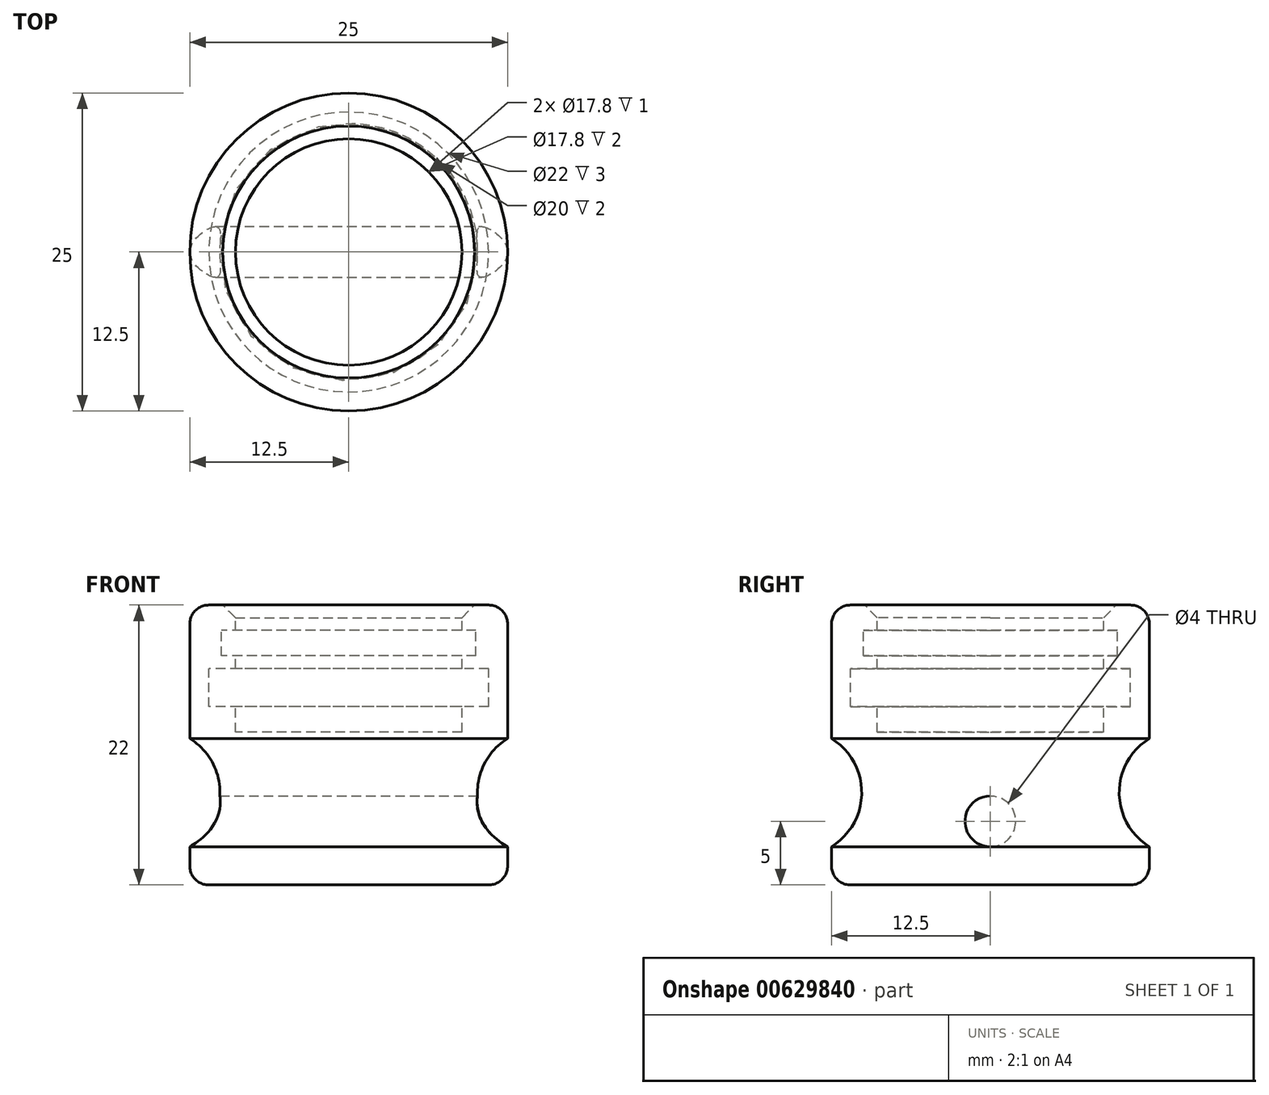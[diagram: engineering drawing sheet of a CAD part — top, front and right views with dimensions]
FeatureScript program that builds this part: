
annotation { "Feature Type Name" : "Feature", "Feature Type Description" : "" }
export const myFeature = defineFeature(function(context is Context, id is Id, definition is map)
    precondition{}
    {
        {
            var Q0;
            Q0=qCreatedBy(makeId("Front.planeOp"),FACE);
            var sketch = newSketch(context, id + "F0", { "sketchPlane" : qUnion([Q0])});
            skLineSegment(sketch, "E0", {"start": v(0, 0) * mm, "end": v(-12.5, 0) * mm});
            skLineSegment(sketch, "E1", {"start": v(-12.5, 0) * mm, "end": v(-12.5, 22) * mm});
            skLineSegment(sketch, "E2", {"start": v(-12.5, 22) * mm, "end": v(-8.9, 22) * mm});
            skLineSegment(sketch, "E3", {"start": v(-8.9, 22) * mm, "end": v(-8.9, 20) * mm});
            skLineSegment(sketch, "E4", {"start": v(-8.9, 20) * mm, "end": v(-10, 20) * mm});
            skLineSegment(sketch, "E5", {"start": v(-10, 20) * mm, "end": v(-10, 18) * mm});
            skLineSegment(sketch, "E6", {"start": v(-10, 18) * mm, "end": v(-8.9, 18) * mm});
            skLineSegment(sketch, "E7", {"start": v(-8.9, 18) * mm, "end": v(-8.9, 17) * mm});
            skLineSegment(sketch, "E8", {"start": v(-8.9, 17) * mm, "end": v(-11, 17) * mm});
            skLineSegment(sketch, "E9", {"start": v(-11, 17) * mm, "end": v(-11, 14) * mm});
            skLineSegment(sketch, "E10", {"start": v(-11, 14) * mm, "end": v(-8.9, 14) * mm});
            skLineSegment(sketch, "E11", {"start": v(-8.9, 14) * mm, "end": v(-8.9, 12) * mm});
            skLineSegment(sketch, "E12", {"start": v(-8.9, 12) * mm, "end": v(0, 12) * mm});
            skLineSegment(sketch, "E13", {"start": v(0, 12) * mm, "end": v(0, 0) * mm});
            skPoint(sketch, "E14", {"position": v(0, 0) * mm});
            skArc(sketch, "E15", {"start": v(-12.5, 3) * mm, "mid": v(-10.12, 7.26) * mm, "end": v(-12.5, 11.51) * mm});
            skSolve(sketch);
        }
        {
            var Q0;
            Q0=makeQuery(id+"F0.imprint","IMPRINT",FACE,{"disambiguationData":[TD([[makeQuery(id+"F0.imprint","IMPRINT",EDGE,{"derivedFrom":sQuery(id+"F0.wireOp",EDGE,"E0")}),-1.0]])]});
            var Q1;
            Q1=sQuery(id+"F0.wireOp",EDGE,"E13");
            revolve(context, id + "F1", {"entities" : qUnion([Q0]), "axis" : qUnion([Q1]), "revolveType" : RevolveType.FULL});
        }
        {
            var Q0;
            Q0=qCreatedBy(makeId("Right.planeOp"),FACE);
            var sketch = newSketch(context, id + "F2", { "sketchPlane" : qUnion([Q0])});
            skCircle(sketch, "E16", {"center": v(0, 5) * mm, "radius": 2 * mm});
            skSolve(sketch);
        }
        {
            var Q0;
            Q0 = qSketchRegion(id + "F2", true);
            extrude(context, id + "F3", {"entities" : qUnion([Q0]), "operationType" : NewBodyOperationType.REMOVE, "endBound" : BoundingType.THROUGH_ALL, "oppositeDirection" : true, "depth" : 25 * mm, "offsetDistance" : 25 * mm, "hasSecondDirection" : true, "secondDirectionBound" : SecondDirectionBoundingType.THROUGH_ALL, "secondDirectionOppositeDirection" : false, "secondDirectionDepth" : 25 * mm});
        }
        {
            var Q0;
            Q0=makeQuery(id+"F1.opRevolve","SWEPT_EDGE",EDGE,{"disambiguationData":[OSD([sQuery(id+"F0.wireOp",EDGE,"E2"),sQuery(id+"F0.wireOp",EDGE,"E3")])]});
            chamfer(context, id + "F4", {"entities" : qUnion([Q0]), "width" : 1 * mm, "tangentPropagation" : true});
        }
        {
            var Q0;
            Q0=makeQuery(id+"F1.opRevolve","SWEPT_EDGE",EDGE,{"disambiguationData":[OSD([sQuery(id+"F0.wireOp",EDGE,"E1"),sQuery(id+"F0.wireOp",EDGE,"E2")])]});
            var Q1;
            Q1=makeQuery(id+"F1.opRevolve","SWEPT_EDGE",EDGE,{"disambiguationData":[OSD([sQuery(id+"F0.wireOp",EDGE,"E0"),sQuery(id+"F0.wireOp",EDGE,"E1")])]});
            fillet(context, id + "F5", {"entities" : qUnion([Q0, Q1]), "radius" : 1.5 * mm, "tangentPropagation" : true, "allowEdgeOverflow" : false});
        }
    });
